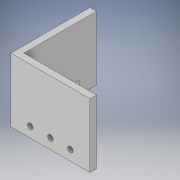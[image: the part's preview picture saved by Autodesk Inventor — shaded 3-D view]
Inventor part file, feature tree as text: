
AUTODESK INVENTOR PART (.ipt)
format: ipt  version: 2019 (Build 230136000, 136)  size: 130,560 bytes
history: native  units: in
note: dims shown in document units (in); Inventor stores cm internally (conversion verified against a paired STEP export)
features: extrude x3, sketch x3
ambient origin geometry x8: Origin, YZ Plane, XZ Plane, XY Plane, X Axis, Y Axis, Z Axis, Center Point
bodies: Solid1 (feature_tree)
feature tree (6):
  extrude  "Extrusion1"  Depth=0.7874in
  extrude  "Extrusion2"  Depth=0.25in
  extrude  "Extrusion3"  Depth=2.4528in TaperAngle=0.0deg
  sketch  "Sketch1"  dims[d0=2.0in d1=0.7874in]
  sketch  "Sketch2"  dims[d2=0.7874in d3=0.25in]
  sketch  "Sketch3"  dims[d4=0.25in d5=2.4528in d6=0.0in d7=0.7874in d8=0.2165in d9=0.75in d10=1.1811in d12=0.7687in d13=0.3937in d15=1.0in d17=2.4528in d18=0.0in d19=0.3937in d20=0.2165in d21=0.75in d22=1.1811in d24=0.7687in d25=0.3937in d27=1.0in d29=2.4528in d30=0.0in]
